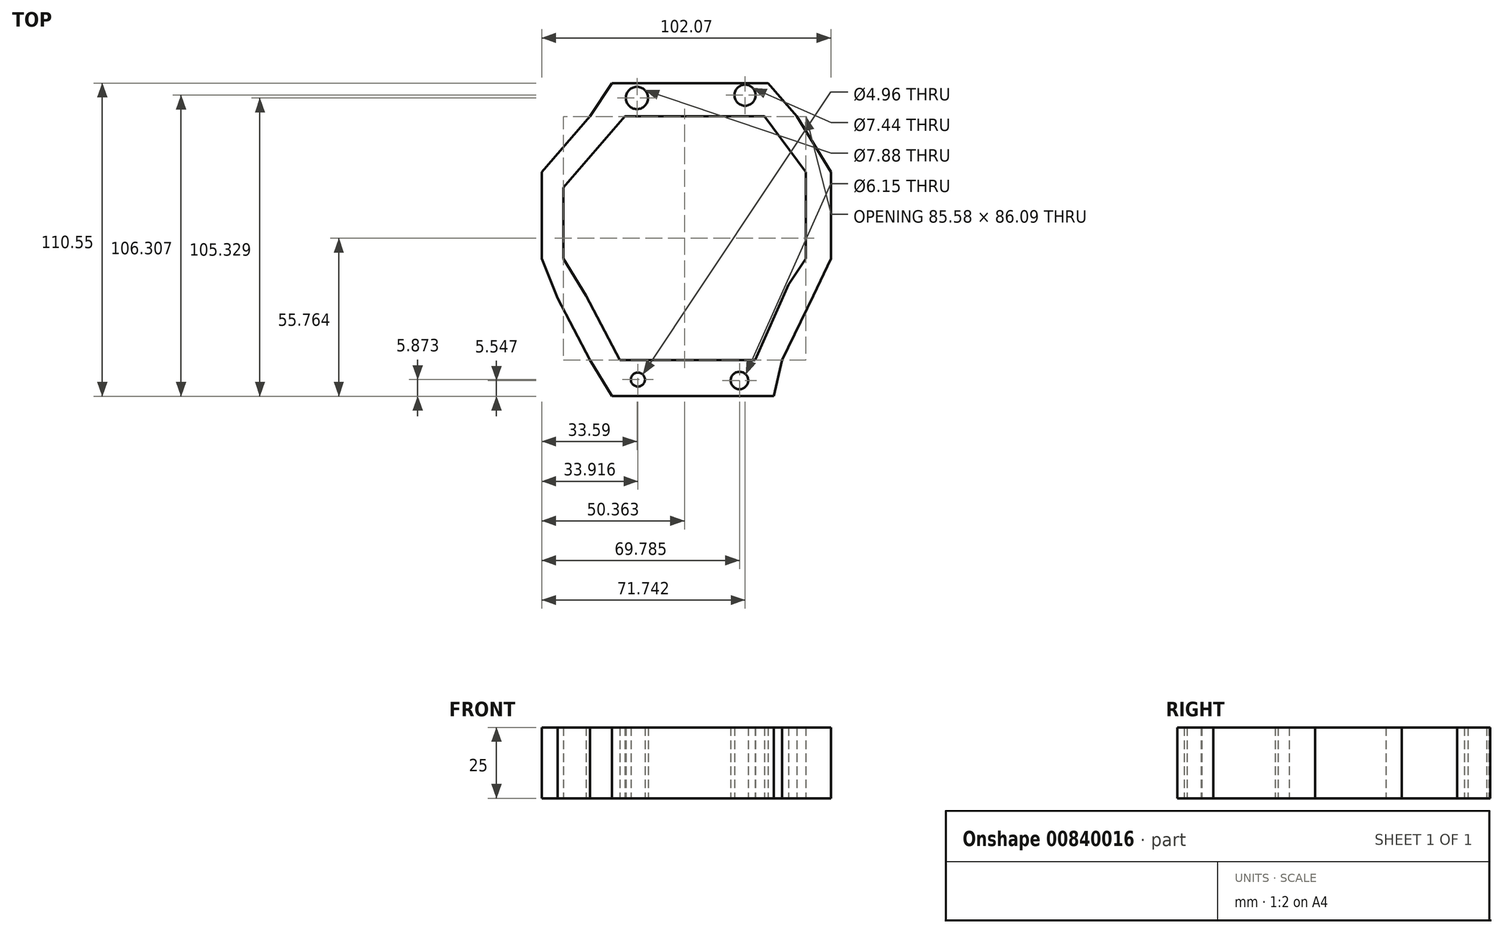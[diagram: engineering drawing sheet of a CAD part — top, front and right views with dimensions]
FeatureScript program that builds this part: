
annotation { "Feature Type Name" : "Feature", "Feature Type Description" : "" }
export const myFeature = defineFeature(function(context is Context, id is Id, definition is map)
    precondition{}
    {
        {
            var Q0;
            Q0=qCreatedBy(makeId("Top.planeOp"),FACE);
            var sketch = newSketch(context, id + "F0", { "sketchPlane" : qUnion([Q0])});
            skLineSegment(sketch, "E0", {"start": v(-29.18, 61.96) * mm, "end": v(25.92, 61.96) * mm});
            skLineSegment(sketch, "E1", {"start": v(25.92, 61.96) * mm, "end": v(36.03, 50.22) * mm});
            skLineSegment(sketch, "E2", {"start": v(36.03, 50.22) * mm, "end": v(-37.01, 50.22) * mm});
            skLineSegment(sketch, "E3", {"start": v(-37.01, 50.22) * mm, "end": v(-29.18, 61.96) * mm});
            skLineSegment(sketch, "E4", {"start": v(-37.01, 50.22) * mm, "end": v(-53.97, 30.65) * mm});
            skLineSegment(sketch, "E5", {"start": v(-53.97, 30.65) * mm, "end": v(-53.97, 0) * mm});
            skLineSegment(sketch, "E6", {"start": v(-53.97, 0) * mm, "end": v(-48.42, -14.02) * mm});
            skLineSegment(sketch, "E7", {"start": v(-48.42, -14.02) * mm, "end": v(-37.01, -35.87) * mm});
            skLineSegment(sketch, "E8", {"start": v(-37.01, -35.87) * mm, "end": v(30.82, -35.87) * mm});
            skLineSegment(sketch, "E9", {"start": v(30.82, -35.87) * mm, "end": v(27.88, -48.59) * mm});
            skLineSegment(sketch, "E10", {"start": v(27.88, -48.59) * mm, "end": v(-29.18, -48.59) * mm});
            skLineSegment(sketch, "E11", {"start": v(-29.18, -48.59) * mm, "end": v(-37.01, -35.87) * mm});
            skLineSegment(sketch, "E12", {"start": v(30.82, -35.87) * mm, "end": v(41.9, -13.04) * mm});
            skLineSegment(sketch, "E13", {"start": v(41.9, -13.04) * mm, "end": v(48.1, 0) * mm});
            skLineSegment(sketch, "E14", {"start": v(48.1, 0) * mm, "end": v(48.1, 30.65) * mm});
            skLineSegment(sketch, "E15", {"start": v(48.1, 30.65) * mm, "end": v(36.03, 50.22) * mm});
            skLineSegment(sketch, "E16", {"start": v(-37.01, 50.22) * mm, "end": v(-29.18, 45) * mm});
            skLineSegment(sketch, "E17", {"start": v(-29.18, 45) * mm, "end": v(-46.4, 25.14) * mm});
            skLineSegment(sketch, "E18", {"start": v(-46.4, 25.14) * mm, "end": v(-53.97, 30.65) * mm});
            skLineSegment(sketch, "E19", {"start": v(-46.4, 25.14) * mm, "end": v(-46.4, 0) * mm});
            skLineSegment(sketch, "E20", {"start": v(-46.4, 0) * mm, "end": v(-38.36, -13.04) * mm});
            skLineSegment(sketch, "E21", {"start": v(-38.36, -13.04) * mm, "end": v(-26.43, -35.87) * mm});
            skLineSegment(sketch, "E22", {"start": v(-26.43, -35.87) * mm, "end": v(21.36, -35.87) * mm});
            skLineSegment(sketch, "E23", {"start": v(21.36, -35.87) * mm, "end": v(33.1, -9.13) * mm});
            skLineSegment(sketch, "E24", {"start": v(33.1, -9.13) * mm, "end": v(39.18, 0) * mm});
            skLineSegment(sketch, "E25", {"start": v(39.18, 0) * mm, "end": v(39.18, 30.65) * mm});
            skLineSegment(sketch, "E26", {"start": v(-29.18, 45) * mm, "end": v(-24.66, 50.22) * mm});
            skLineSegment(sketch, "E27", {"start": v(39.18, 30.65) * mm, "end": v(24.62, 50.22) * mm});
            skLineSegment(sketch, "E28", {"start": v(24.62, 50.22) * mm, "end": v(28.67, 44.78) * mm});
            skLineSegment(sketch, "E29", {"start": v(28.67, 44.78) * mm, "end": v(36.03, 50.22) * mm});
            skCircle(sketch, "E30", {"center": v(-20.05, -42.72) * mm, "radius": 2.48 * mm});
            skCircle(sketch, "E31", {"center": v(15.82, -43.04) * mm, "radius": 3.08 * mm});
            skCircle(sketch, "E32", {"center": v(-20.38, 56.74) * mm, "radius": 3.94 * mm});
            skCircle(sketch, "E33", {"center": v(17.77, 57.72) * mm, "radius": 3.72 * mm});
            skSolve(sketch);
        }
        {
            var Q0;
            Q0 = qSketchRegion(id + "F0", true);
            extrude(context, id + "F1", {"entities" : qUnion([Q0]), "depth" : 25 * mm, "offsetDistance" : 25 * mm});
        }
    });
